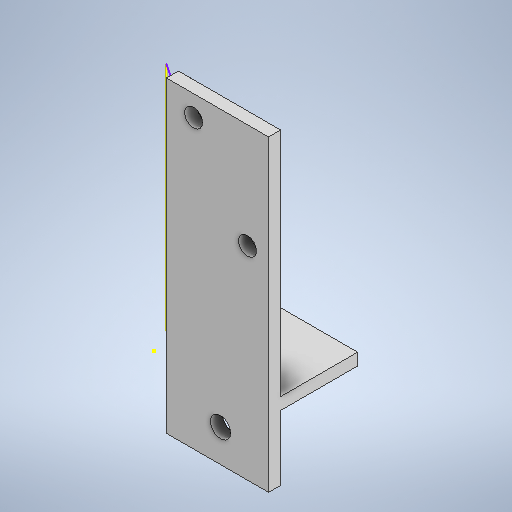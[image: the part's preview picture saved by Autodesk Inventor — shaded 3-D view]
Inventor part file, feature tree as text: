
AUTODESK INVENTOR PART (.ipt)
format: ipt  version: 2025.1 (Build 291241000, 241)  size: 302,592 bytes
history: native  units: in
note: dims shown in document units (in); Inventor stores cm internally (conversion verified against a paired STEP export)
features: extrude x7, sketch x6, move_body x4, direct_edit x2
ambient origin geometry x8: Origin, YZ Plane, XZ Plane, XY Plane, X Axis, Y Axis, Z Axis, Center Point
bodies: Solid1 (feature_tree)
feature tree (19):
  extrude  "Extrusion1"  Depth=0.8in
  extrude  "Extrusion2"  Depth=0.125in
  extrude  "Extrusion3"  Depth=0.125in
  extrude  "Extrusion4"  Depth=2.4in TaperAngle=0.0deg
  extrude  "Extrusion7"  Depth=1.8125in TaperAngle=0.0deg
  direct_edit  "Direct Edit1"
  direct_edit  "Direct Edit8"
  sketch  "Sketch16"  dims[d39=0.0in d40=0.0in d41=0.125in d76=0.395in d77=0.395in d78=1.55in d79=0.115in d80=0.115in d81=0.215in d82=0.46in d83=0.1875in d84=0.1875in d99=0.0in d100=0.0in d101=0.1875in d107=0.25in d108=0.0in d109=0.0in d110=0.0in d111=-0.0625in d112=0.125in d113=0.0in d114=0.0in d115=0.0in d116=-0.063in d42=0.0in]
  extrude  "Extrusion18"  Depth=0.125in
  extrude  "Extrusion19"  Depth=0.125in
  sketch  "Sketch1"  dims[d0=1.0in d1=0.8in]
  sketch  "Sketch2"  dims[d2=0.1245in d3=0.0in d4=0.125in]
  sketch  "Sketch3"  dims[d5=0.675in d6=0.0in d7=0.125in]
  sketch  "Sketch4"  dims[d8=2.4in d9=0.0in d16=2.5in d17=0.0in]
  sketch  "Sketch7"  dims[d23=0.21in d24=1.8125in d25=0.0in]
  move_body  "Move1"
  move_body  "Move11"
  move_body  "Move13"
  move_body  "Move14"
